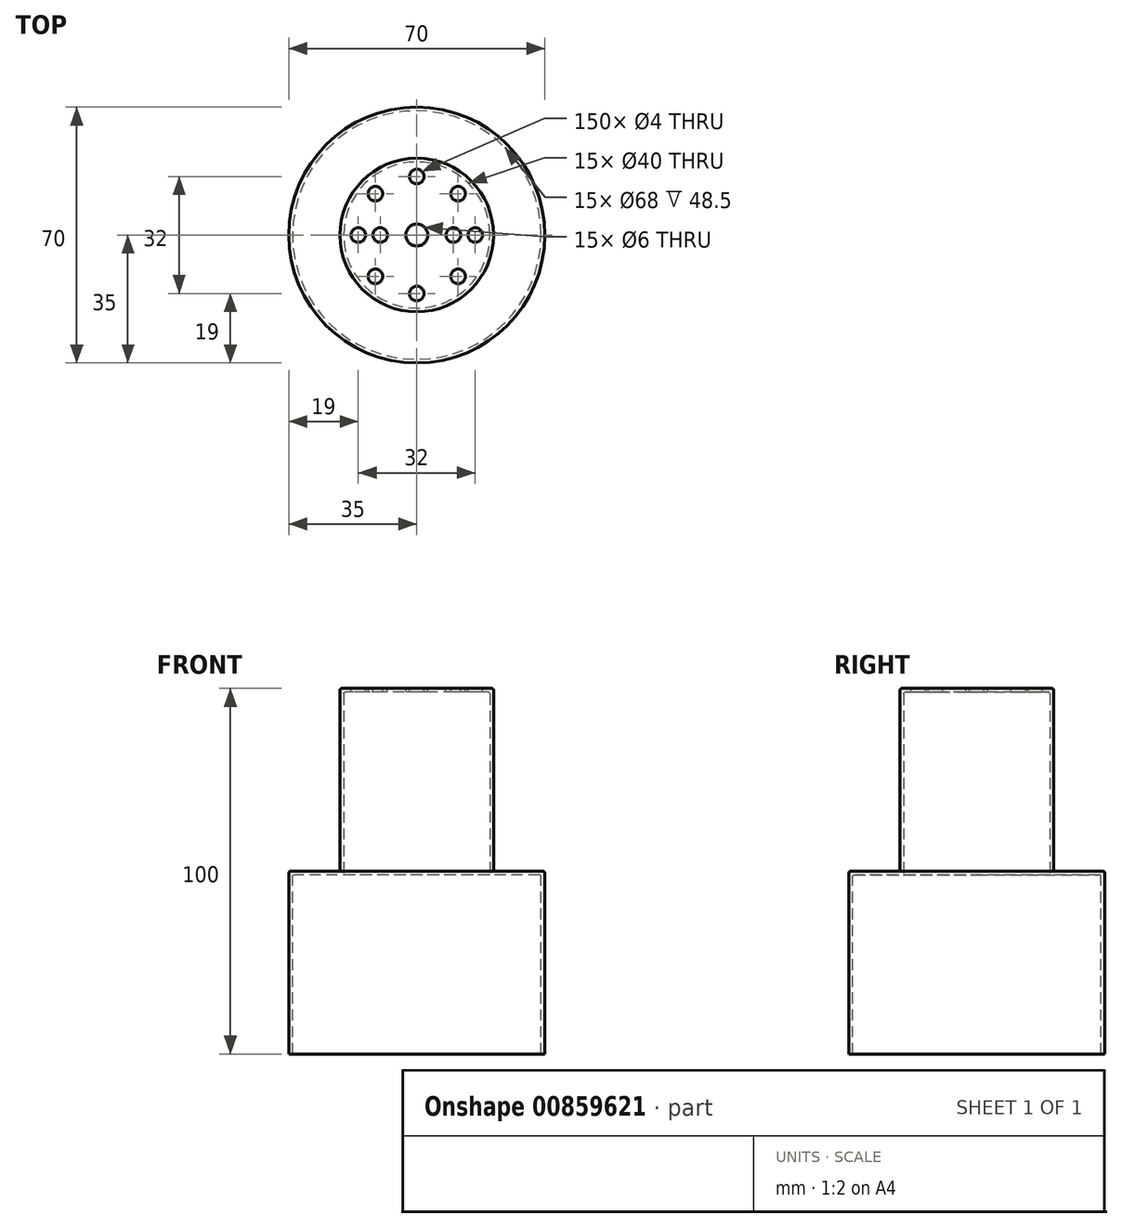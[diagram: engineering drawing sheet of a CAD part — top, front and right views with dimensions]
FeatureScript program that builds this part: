
annotation { "Feature Type Name" : "Feature", "Feature Type Description" : "" }
export const myFeature = defineFeature(function(context is Context, id is Id, definition is map)
    precondition{}
    {
        {
            var Q0;
            Q0=qCreatedBy(makeId("Top.planeOp"),FACE);
            var sketch = newSketch(context, id + "F0", { "sketchPlane" : qUnion([Q0])});
            skCircle(sketch, "E0", {"center": v(0, 0) * mm, "radius": 35 * mm});
            skCircle(sketch, "E1", {"center": v(0, 0) * mm, "radius": 21 * mm});
            skSolve(sketch);
        }
        {
            var Q0;
            Q0=makeQuery(id+"F0.imprint","IMPRINT",FACE,{"disambiguationData":[TD([[makeQuery(id+"F0.imprint","IMPRINT",EDGE,{"derivedFrom":sQuery(id+"F0.wireOp",EDGE,"E1")}),1.0]])]});
            extrude(context, id + "F1", {"entities" : qUnion([Q0]), "endBound" : BoundingType.SYMMETRIC, "depth" : 100 * mm, "offsetDistance" : 25 * mm});
        }
        {
            var Q0;
            Q0=makeQuery(id+"F0.imprint","IMPRINT",FACE,{"disambiguationData":[TD([[makeQuery(id+"F0.imprint","IMPRINT",EDGE,{"derivedFrom":sQuery(id+"F0.wireOp",EDGE,"E0")}),1.0]])]});
            extrude(context, id + "F2", {"entities" : qUnion([Q0]), "depth" : -50 * mm, "offsetDistance" : 25 * mm});
        }
        {
            var Q0;
            Q0=makeQuery(id+"F1.opExtrude","SWEPT_BODY",BODY,{"disambiguationData":[OSD([sQuery(id+"F0.wireOp",EDGE,"E1")])]});
            var Q1;
            Q1=makeQuery(id+"F2.opExtrude","SWEPT_BODY",BODY,{"disambiguationData":[OSD([sQuery(id+"F0.wireOp",EDGE,"E0"),sQuery(id+"F0.wireOp",EDGE,"E1")])]});
            booleanBodies(context, id + "F3", {"operationType" : BooleanOperationType.UNION, "tools" : qUnion([Q0, Q1])});
        }
        {
            var Q0;
            {var subQ0=sQuery(id+"F0.wireOp",EDGE,"E1");Q0=makeQuery(id+"F3.opBoolean","MERGE",FACE,{"derivedFrom":[makeQuery(id+"F1.opExtrude","CAP_FACE",FACE,{"disambiguationData":[OSD([subQ0])],"isStart":true}),makeQuery(id+"F2.opExtrude","CAP_FACE",FACE,{"disambiguationData":[OSD([sQuery(id+"F0.wireOp",EDGE,"E0"),subQ0])],"isStart":false})]});}
            shell(context, id + "F4", {"entities" : qUnion([Q0]), "thickness" : 1 * mm});
        }
        {
            var Q0;
            Q0=makeQuery(id+"F2.opExtrude","CAP_EDGE",EDGE,{"disambiguationData":[OSD([sQuery(id+"F0.wireOp",EDGE,"E0")])],"isStart":true});
            var Q1;
            Q1=makeQuery(id+"F2.opExtrude","CAP_EDGE",EDGE,{"disambiguationData":[OSD([sQuery(id+"F0.wireOp",EDGE,"E1")])],"isStart":true});
            var Q2;
            Q2=makeQuery(id+"F1.opExtrude","CAP_EDGE",EDGE,{"disambiguationData":[OSD([sQuery(id+"F0.wireOp",EDGE,"E1")])],"isStart":false});
            var Q3;
            {var subQ0=sQuery(id+"F0.wireOp",EDGE,"E0");Q3=makeQuery(id+"F4.opShell","OFFSET_EDGE",EDGE,{"disambiguationData":[OSD([subQ0]),TDD([makeQuery(id+"F2.opExtrude","CAP_EDGE",EDGE,{"disambiguationData":[OSD([subQ0])],"isStart":true})])]});}
            var Q4;
            {var subQ0=sQuery(id+"F0.wireOp",EDGE,"E1");Q4=makeQuery(id+"F4.opShell","OFFSET_EDGE",EDGE,{"disambiguationData":[OSD([subQ0]),TDD([makeQuery(id+"F2.opExtrude","CAP_EDGE",EDGE,{"disambiguationData":[OSD([subQ0])],"isStart":true})])]});}
            var Q5;
            {var subQ0=sQuery(id+"F0.wireOp",EDGE,"E1");Q5=makeQuery(id+"F4.opShell","OFFSET_EDGE",EDGE,{"disambiguationData":[OSD([subQ0]),TDD([makeQuery(id+"F1.opExtrude","CAP_EDGE",EDGE,{"disambiguationData":[OSD([subQ0])],"isStart":false})])]});}
            fillet(context, id + "F5", {"entities" : qUnion([Q0, Q1, Q2, Q3, Q4, Q5]), "radius" : 0.5 * mm, "tangentPropagation" : true, "allowEdgeOverflow" : false});
        }
        {
            var Q0;
            Q0=makeQuery(id+"F1.opExtrude","CAP_FACE",FACE,{"disambiguationData":[OSD([sQuery(id+"F0.wireOp",EDGE,"E1")])],"isStart":false});
            var sketch = newSketch(context, id + "F6", { "sketchPlane" : qUnion([Q0])});
            skLineSegment(sketch, "E2.left", {"start": v(10, 0) * mm, "end": v(10, 0) * mm});
            skLineSegment(sketch, "E2.right", {"start": v(-10, 0) * mm, "end": v(-10, 0) * mm});
            skPoint(sketch, "E2.middle", {"position": v(0, 0) * mm});
            skCircle(sketch, "E3", {"center": v(10, 0) * mm, "radius": 2 * mm});
            skCircle(sketch, "E4", {"center": v(-10, 0) * mm, "radius": 2 * mm});
            skCircle(sketch, "E5", {"center": v(0, 16) * mm, "radius": 2 * mm});
            skCircle(sketch, "E6", {"center": v(0, -16) * mm, "radius": 2 * mm});
            skCircle(sketch, "E7", {"center": v(16, 0) * mm, "radius": 2 * mm});
            skCircle(sketch, "E8", {"center": v(-16, 0) * mm, "radius": 2 * mm});
            skCircle(sketch, "E9", {"center": v(11.31, 11.31) * mm, "radius": 2 * mm});
            skCircle(sketch, "E10", {"center": v(-11.31, -11.31) * mm, "radius": 2 * mm});
            skCircle(sketch, "E11", {"center": v(11.31, -11.31) * mm, "radius": 2 * mm});
            skCircle(sketch, "E12", {"center": v(-11.31, 11.31) * mm, "radius": 2 * mm});
            skCircle(sketch, "E13", {"center": v(0, 0) * mm, "radius": 3 * mm});
            skSolve(sketch);
        }
        {
            var Q0;
            Q0=makeQuery(id+"F6.imprint","IMPRINT",FACE,{"disambiguationData":[TD([[makeQuery(id+"F6.imprint","IMPRINT",EDGE,{"derivedFrom":sQuery(id+"F6.wireOp",EDGE,"E12")}),1.0]])]});
            var Q1;
            Q1=makeQuery(id+"F6.imprint","IMPRINT",FACE,{"disambiguationData":[TD([[makeQuery(id+"F6.imprint","IMPRINT",EDGE,{"derivedFrom":sQuery(id+"F6.wireOp",EDGE,"E5")}),1.0]])]});
            var Q2;
            Q2=makeQuery(id+"F6.imprint","IMPRINT",FACE,{"disambiguationData":[TD([[makeQuery(id+"F6.imprint","IMPRINT",EDGE,{"derivedFrom":sQuery(id+"F6.wireOp",EDGE,"E9")}),1.0]])]});
            var Q3;
            Q3=makeQuery(id+"F6.imprint","IMPRINT",FACE,{"disambiguationData":[TD([[makeQuery(id+"F6.imprint","IMPRINT",EDGE,{"derivedFrom":sQuery(id+"F6.wireOp",EDGE,"E3")}),1.0]])]});
            var Q4;
            Q4=makeQuery(id+"F6.imprint","IMPRINT",FACE,{"disambiguationData":[TD([[makeQuery(id+"F6.imprint","IMPRINT",EDGE,{"derivedFrom":sQuery(id+"F6.wireOp",EDGE,"E4")}),1.0]])]});
            var Q5;
            Q5=makeQuery(id+"F6.imprint","IMPRINT",FACE,{"disambiguationData":[TD([[makeQuery(id+"F6.imprint","IMPRINT",EDGE,{"derivedFrom":sQuery(id+"F6.wireOp",EDGE,"E8")}),1.0]])]});
            var Q6;
            Q6=makeQuery(id+"F6.imprint","IMPRINT",FACE,{"disambiguationData":[TD([[makeQuery(id+"F6.imprint","IMPRINT",EDGE,{"derivedFrom":sQuery(id+"F6.wireOp",EDGE,"E7")}),1.0]])]});
            var Q7;
            Q7=makeQuery(id+"F6.imprint","IMPRINT",FACE,{"disambiguationData":[TD([[makeQuery(id+"F6.imprint","IMPRINT",EDGE,{"derivedFrom":sQuery(id+"F6.wireOp",EDGE,"E11")}),1.0]])]});
            var Q8;
            Q8=makeQuery(id+"F6.imprint","IMPRINT",FACE,{"disambiguationData":[TD([[makeQuery(id+"F6.imprint","IMPRINT",EDGE,{"derivedFrom":sQuery(id+"F6.wireOp",EDGE,"E6")}),1.0]])]});
            var Q9;
            Q9=makeQuery(id+"F6.imprint","IMPRINT",FACE,{"disambiguationData":[TD([[makeQuery(id+"F6.imprint","IMPRINT",EDGE,{"derivedFrom":sQuery(id+"F6.wireOp",EDGE,"E10")}),1.0]])]});
            var Q10;
            Q10=makeQuery(id+"F6.imprint","IMPRINT",FACE,{"disambiguationData":[TD([[makeQuery(id+"F6.imprint","IMPRINT",EDGE,{"derivedFrom":sQuery(id+"F6.wireOp",EDGE,"E13")}),1.0]])]});
            extrude(context, id + "F7", {"entities" : qUnion([Q0, Q1, Q2, Q3, Q4, Q5, Q6, Q7, Q8, Q9, Q10]), "operationType" : NewBodyOperationType.REMOVE, "oppositeDirection" : true, "depth" : 25 * mm, "offsetDistance" : 25 * mm});
        }
    });
